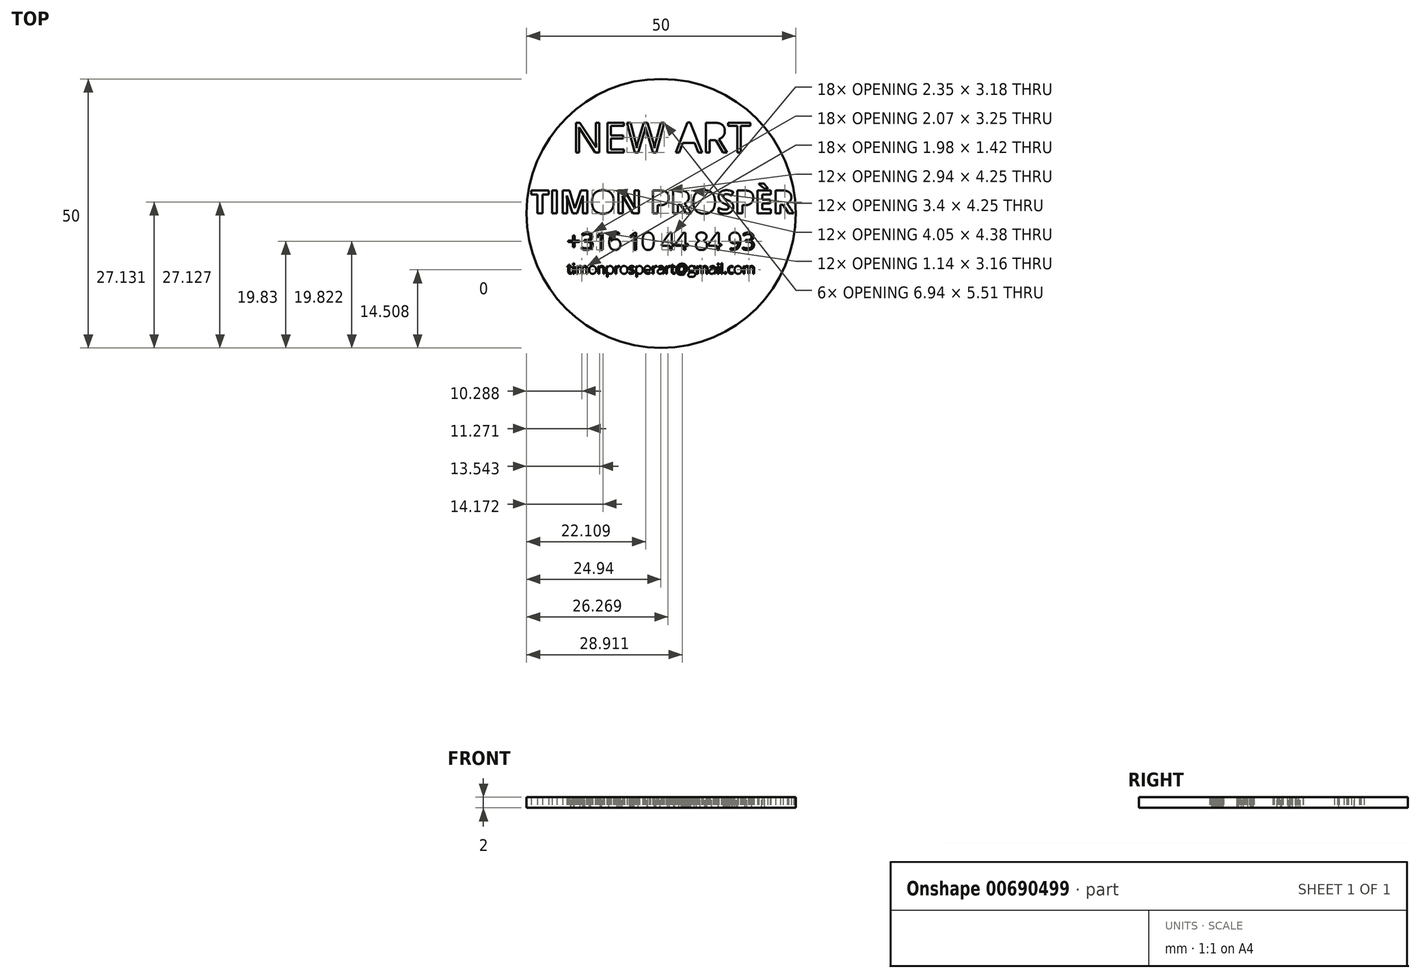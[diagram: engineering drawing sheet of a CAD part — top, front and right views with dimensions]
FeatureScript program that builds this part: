
annotation { "Feature Type Name" : "Feature", "Feature Type Description" : "" }
export const myFeature = defineFeature(function(context is Context, id is Id, definition is map)
    precondition{}
    {
        {
            var Q0;
            Q0=qCreatedBy(makeId("Top.planeOp"),FACE);
            var sketch = newSketch(context, id + "F0", { "sketchPlane" : qUnion([Q0])});
            skCircle(sketch, "E0", {"center": v(0, 0) * mm, "radius": 25 * mm});
            skText(sketch, "E1", { "text": "TIMON PROSPÈR", "fontName": "OpenSans-Bold.ttf"});
            skText(sketch, "E2", { "text": "+316 10 44 84 93", "fontName": "OpenSans-Regular.ttf"});
            skText(sketch, "E3", { "text": "<email>", "fontName": "OpenSans-Regular.ttf"});
            skText(sketch, "E4", { "text": "NEW ART", "fontName": "OpenSans-Regular.ttf"});
            const initialGuessF0  = {"E1": [-0.02424, 0, 1, 0, 0.00429], "E2": [-0.0175, -0.00676, 1, 0, 0.00319], "E3": [-0.0175, -0.0112, 1, 0, 0.00187], "E4": [-0.01658, 0.01134, 1, 0, 0.00556]};
            skSetInitialGuess(sketch, initialGuessF0);
            skSolve(sketch);
        }
        {
            var Q0;
            Q0 = qSketchRegion(id + "F0", true);
            extrude(context, id + "F1", {"entities" : qUnion([Q0]), "depth" : 2 * mm, "offsetDistance" : 25 * mm});
        }
    });
